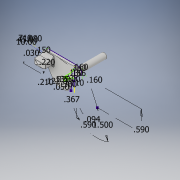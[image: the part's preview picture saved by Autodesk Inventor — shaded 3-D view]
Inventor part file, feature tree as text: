
AUTODESK INVENTOR PART (.ipt)
format: ipt  version: 2018.3 (Build 223284000, 284)  size: 348,160 bytes
history: native  units: in
note: dims shown in document units (in); Inventor stores cm internally (conversion verified against a paired STEP export)
features: extrude x7, sketch x4, fillet x2, revolve x1, plane x1
ambient origin geometry x8: Origin, YZ Plane, XZ Plane, XY Plane, X Axis, Y Axis, Z Axis, Center Point
bodies: Solid1 (feature_tree)
feature tree (15):
  sketch  "Sketch1"  dims[d0=0.1555in d1=0.16in]
  extrude  "Extrusion1"  Depth=0.16in
  extrude  "Extrusion2"  Depth=0.08in
  revolve  "Revolution1"  Angle=135.0deg
  extrude  "Extrusion3"  Depth=0.8383in
  sketch  "Sketch3"  dims[d5=0.71in d6=135.0deg]
  extrude  "Extrusion4"  Depth=0.21in
  extrude  "Extrusion5"  Depth=0.05in
  plane  "Work Plane1"
  extrude  "Extrusion6"  Depth=0.22in
  fillet  "Fillet1"  Radius=0.0687in
  extrude  "Extrusion7"  TaperAngle=45.0deg  [1 undecoded]
  fillet  "Fillet2"  Radius=0.03in
  sketch  "Sketch2"  dims[d2=0.16in d3=0.08in]
  sketch  "Sketch4"  dims[d9=0.367in d10=0.8383in d11=0.21in d12=0.05in d13=0.22in d14=0.0687in d15=45.0deg d16=0.03in d17=0.15in d18=1.5in d19=0.59in d20=0.59in d21=0.094in d22=0.14in d23=0.07in d24=0.0in d25=0.07in d26=0.825in d27=0.0in d28=0.0in d29=0.18in d30=90.0deg d31=0.07in d32=0.307in d33=0.0in d34=0.0in d35=0.03in d36=0.13in d37=0.3in d38=0.16in d39=0.11in d40=0.875in d41=0.0in d42=0.57in d43=0.0in d44=0.0in d45=0.54in d46=0.57in d47=0.0in d48=0.0145in d49=0.57in d50=0.0in d51=0.0145in]
note: 1 required parameter value undecoded (feature->parameter linkage not recoverable at this tier; creation-order binding heuristic only, values carry confidence <= 0.55)
